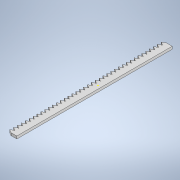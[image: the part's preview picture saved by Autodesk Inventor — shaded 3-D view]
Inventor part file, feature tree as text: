
AUTODESK INVENTOR PART (.ipt)
format: ipt  version: 2020 (Build 240168000, 168)  size: 302,080 bytes
history: native  units: mm
features: sketch x8, extrude x6, pattern_linear x2
ambient origin geometry x8: Origin, YZ Plane, XZ Plane, XY Plane, X Axis, Y Axis, Z Axis, Center Point
bodies: Solid1 (feature_tree)
feature tree (16):
  extrude  "Extrusion1"  Depth=110.0mm
  extrude  "Extrusion2"  Depth=55.0mm
  pattern_linear  "Rectangular Pattern1"  Count1=55 Spacing1=2.0mm
  extrude  "Extrusion3"  Depth=10.0mm TaperAngle=0.0deg
  extrude  "Extrusion4"  Depth=400.0mm
  pattern_linear  "Rectangular Pattern2"  Spacing1=10.0mm  [1 undecoded]
  extrude  "Extrusion5"  Depth=10.0mm TaperAngle=0.0deg
  sketch  "Sketch6"  dims[d8=2.0mm d9=0.0mm d10=550.0mm d12=2.0mm]
  extrude  "Extrusion6"  [1 undecoded]
  sketch  "Sketch8"  dims[d17=10.0mm d18=0.0mm d19=400.0mm d21=3.0mm d22=10.0mm d23=0.0mm d24=10.0mm d25=0.0mm]
  sketch  "Sketch1"  dims[d0=4.5mm d1=110.0mm]
  sketch  "Sketch2"  dims[d2=2.25mm d3=55.0mm]
  sketch  "Sketch3"  dims[d4=2.0mm d5=0.0mm]
  sketch  "Sketch4"  dims[d6=0.263mm]
  sketch  "Sketch5"  dims[d7=1.0mm]
  sketch  "Sketch7"  dims[d13=3.0mm d15=10.0mm d16=0.0mm]
note: 2 required parameter values undecoded (feature->parameter linkage not recoverable at this tier; creation-order binding heuristic only, values carry confidence <= 0.55)
